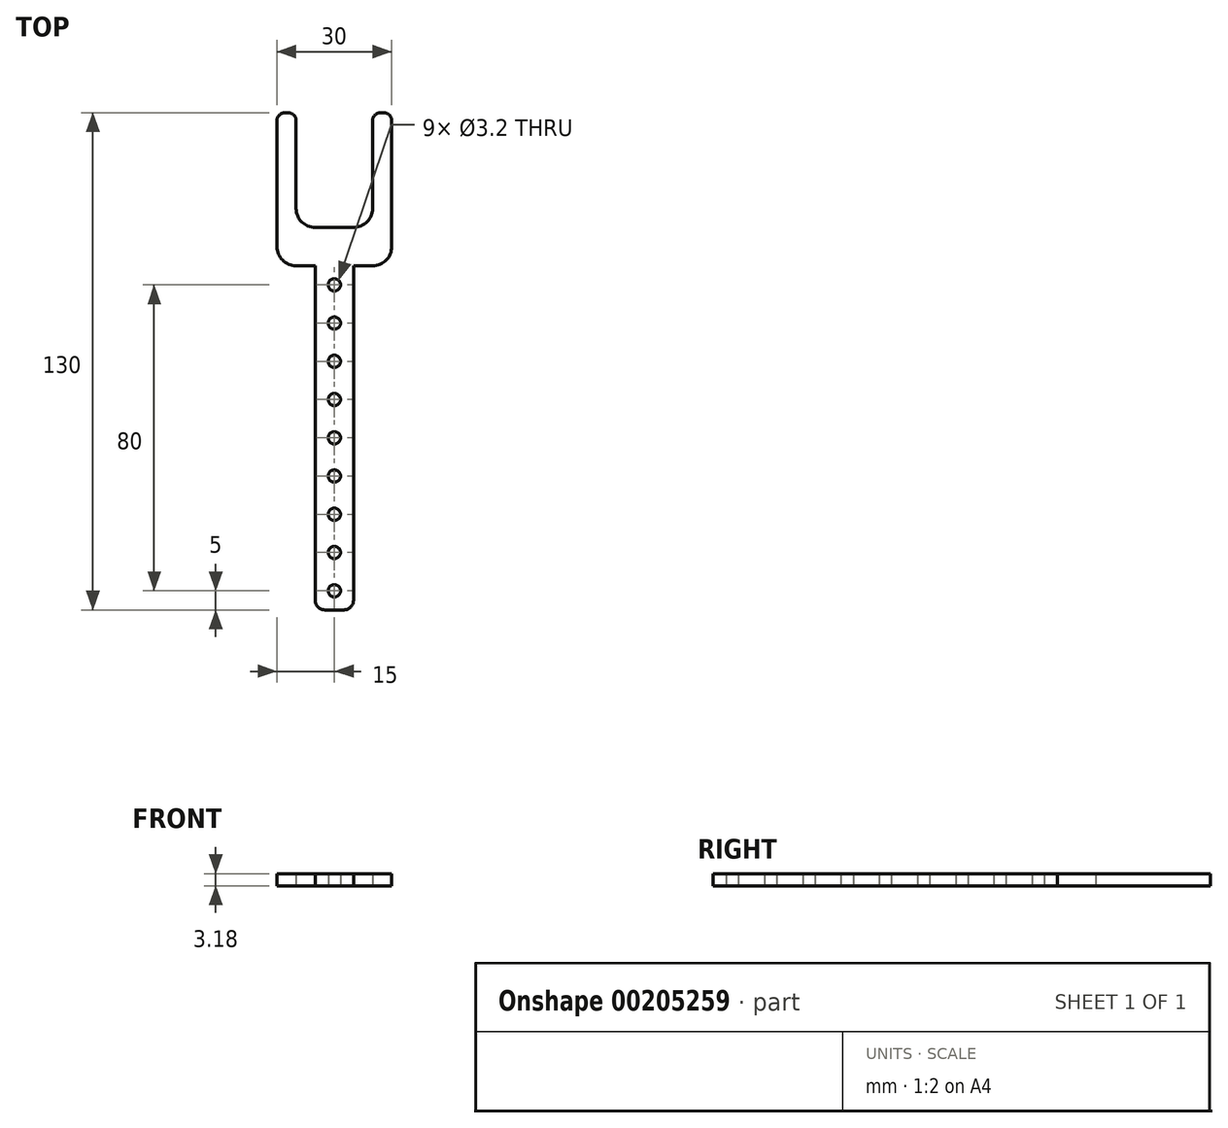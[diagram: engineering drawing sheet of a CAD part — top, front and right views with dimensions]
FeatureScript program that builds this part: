
annotation { "Feature Type Name" : "Feature", "Feature Type Description" : "" }
export const myFeature = defineFeature(function(context is Context, id is Id, definition is map)
    precondition{}
    {
        {
            var Q0;
            Q0=qCreatedBy(makeId("Top.planeOp"),FACE);
            var sketch = newSketch(context, id + "F0", { "sketchPlane" : qUnion([Q0])});
            skLineSegment(sketch, "E0.bottom", {"start": v(-10, 0) * mm, "end": v(-5, 0) * mm});
            skLineSegment(sketch, "E0.top", {"start": v(-5, 10) * mm, "end": v(5, 10) * mm});
            skLineSegment(sketch, "E0.left", {"start": v(-15, 5) * mm, "end": v(-15, 10) * mm});
            skLineSegment(sketch, "E0.right", {"start": v(15, 5) * mm, "end": v(15, 10) * mm});
            skLineSegment(sketch, "E1.top", {"start": v(-13, 40) * mm, "end": v(-12, 40) * mm});
            skLineSegment(sketch, "E1.left", {"start": v(-15, 10) * mm, "end": v(-15, 38) * mm});
            skLineSegment(sketch, "E1.right", {"start": v(-10, 15) * mm, "end": v(-10, 38) * mm});
            skLineSegment(sketch, "E2.MirrorCS", {"start": v(10, 15) * mm, "end": v(10, 38) * mm});
            skLineSegment(sketch, "E3.MirrorCS", {"start": v(15, 10) * mm, "end": v(15, 38) * mm});
            skLineSegment(sketch, "E4.MirrorCS", {"start": v(13, 40) * mm, "end": v(12, 40) * mm});
            skLineSegment(sketch, "E5.top", {"start": v(0, -90) * mm, "end": v(-2.5, -90) * mm});
            skLineSegment(sketch, "E5.right", {"start": v(-5, 0) * mm, "end": v(-5, -87.5) * mm});
            skLineSegment(sketch, "E6.MirrorCS", {"start": v(5, 0) * mm, "end": v(5, -87.5) * mm});
            skLineSegment(sketch, "E7.MirrorCS", {"start": v(0, -90) * mm, "end": v(2.5, -90) * mm});
            skLineSegment(sketch, "E8.trimOffspring", {"start": v(5, 0) * mm, "end": v(10, 0) * mm});
            skPoint(sketch, "E1.bottom.end.orphan", {"position": v(-10, 0) * mm});
            skPoint(sketch, "E9.orphan", {"position": v(10, 0) * mm});
            skCircle(sketch, "E10", {"center": v(0, -5) * mm, "radius": 1.6 * mm});
            skCircle(sketch, "E11.0.1.0", {"center": v(0, -15) * mm, "radius": 1.6 * mm});
            skCircle(sketch, "E11.0.2.0", {"center": v(0, -25) * mm, "radius": 1.6 * mm});
            skCircle(sketch, "E11.0.3.0", {"center": v(0, -35) * mm, "radius": 1.6 * mm});
            skLineSegment(sketch, "E11.direction1", {"start": v(0, -5) * mm, "end": v(25, -5) * mm, "construction": true});
            skLineSegment(sketch, "E11.direction2", {"start": v(0, -5) * mm, "end": v(0, -15) * mm, "construction": true});
            skArc(sketch, "E12", {"start": v(-15, 5) * mm, "mid": v(-13.54, 1.46) * mm, "end": v(-10, 0) * mm});
            skPoint(sketch, "E13.orphan", {"position": v(-15, 0) * mm});
            skArc(sketch, "E14", {"start": v(-10, 15) * mm, "mid": v(-8.54, 11.46) * mm, "end": v(-5, 10) * mm});
            skArc(sketch, "E15", {"start": v(-13, 40) * mm, "mid": v(-14.41, 39.41) * mm, "end": v(-15, 38) * mm});
            skPoint(sketch, "E16.orphan", {"position": v(-15, 40) * mm});
            skArc(sketch, "E17.MirrorCS", {"start": v(-12, 40) * mm, "mid": v(-10.59, 39.41) * mm, "end": v(-10, 38) * mm});
            skPoint(sketch, "E18.orphan", {"position": v(-10, 40) * mm});
            skArc(sketch, "E19.MirrorCS", {"start": v(12, 40) * mm, "mid": v(10.59, 39.41) * mm, "end": v(10, 38) * mm});
            skArc(sketch, "E20.MirrorCS", {"start": v(13, 40) * mm, "mid": v(14.41, 39.41) * mm, "end": v(15, 38) * mm});
            skArc(sketch, "E21.MirrorCS", {"start": v(10, 15) * mm, "mid": v(8.54, 11.46) * mm, "end": v(5, 10) * mm});
            skArc(sketch, "E22.MirrorCS", {"start": v(15, 5) * mm, "mid": v(13.54, 1.46) * mm, "end": v(10, 0) * mm});
            skPoint(sketch, "E23.orphan", {"position": v(10, 40) * mm});
            skPoint(sketch, "E24.orphan", {"position": v(15, 40) * mm});
            skPoint(sketch, "E25.orphan", {"position": v(15, 0) * mm});
            skArc(sketch, "E26", {"start": v(-5, -87.5) * mm, "mid": v(-4.27, -89.27) * mm, "end": v(-2.5, -90) * mm});
            skPoint(sketch, "E27.orphan", {"position": v(-5, -90) * mm});
            skArc(sketch, "E28.MirrorCS", {"start": v(5, -87.5) * mm, "mid": v(4.27, -89.27) * mm, "end": v(2.5, -90) * mm});
            skCircle(sketch, "E29.0.0.4", {"center": v(0, -45) * mm, "radius": 1.6 * mm});
            skCircle(sketch, "E29.0.0.5", {"center": v(0, -55) * mm, "radius": 1.6 * mm});
            skCircle(sketch, "E29.0.0.6", {"center": v(0, -65) * mm, "radius": 1.6 * mm});
            skCircle(sketch, "E29.0.0.7", {"center": v(0, -75) * mm, "radius": 1.6 * mm});
            skCircle(sketch, "E29.0.0.8", {"center": v(0, -85) * mm, "radius": 1.6 * mm});
            skSolve(sketch);
        }
        {
            var Q0;
            Q0 = qSketchRegion(id + "F0", true);
            extrude(context, id + "F1", {"entities" : qUnion([Q0]), "depth" : 3.17 * mm});
        }
    });
